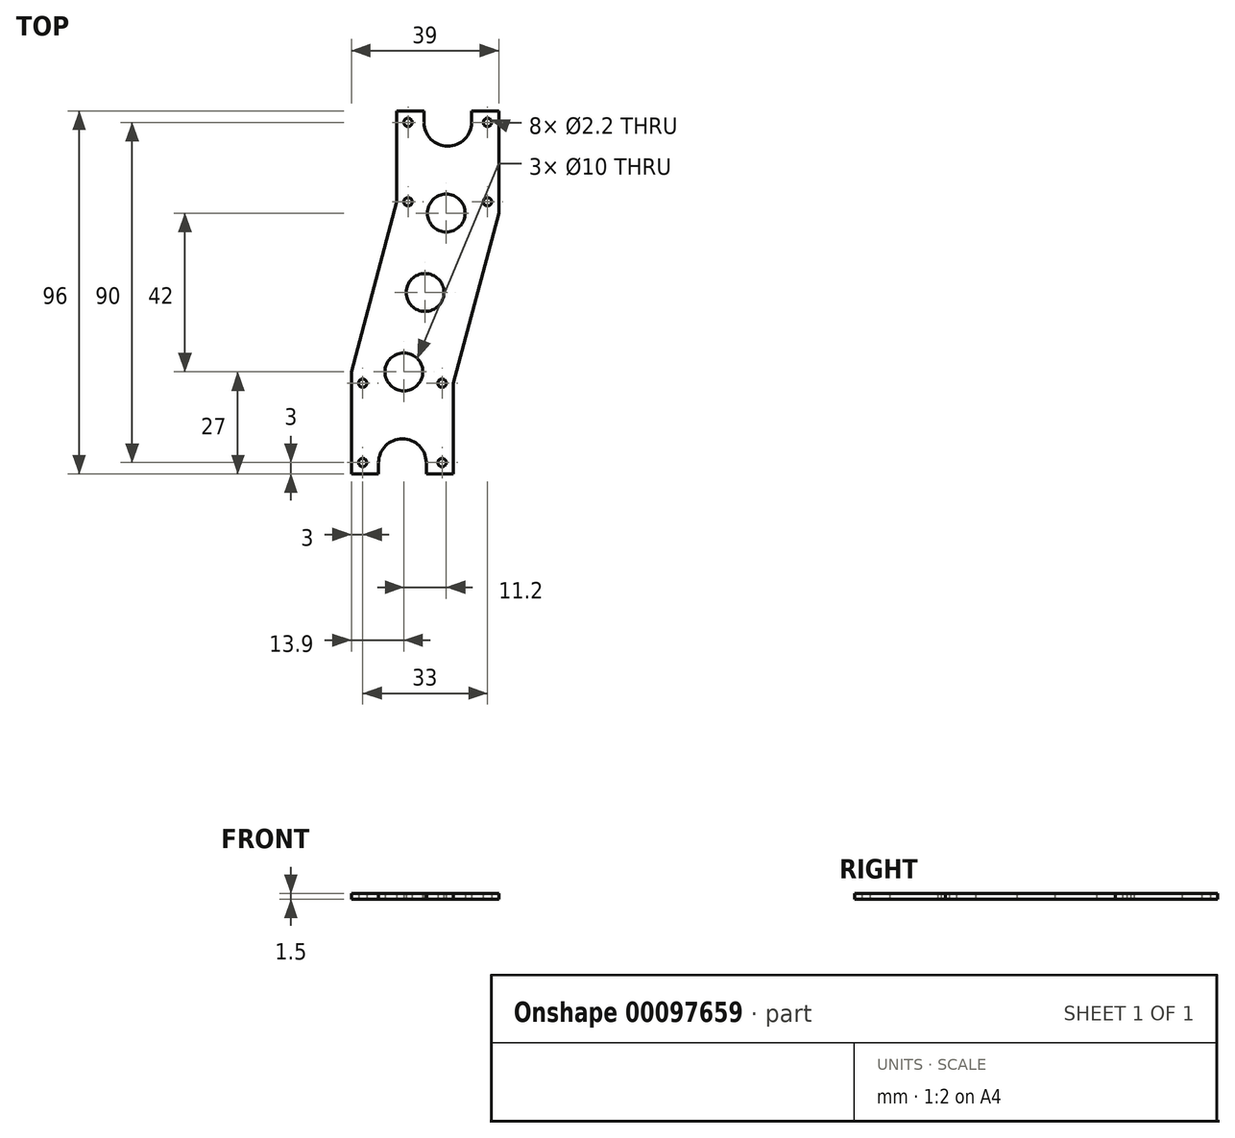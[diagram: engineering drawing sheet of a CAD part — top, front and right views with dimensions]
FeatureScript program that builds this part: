
annotation { "Feature Type Name" : "Feature", "Feature Type Description" : "" }
export const myFeature = defineFeature(function(context is Context, id is Id, definition is map)
    precondition{}
    {
        {
            var Q0;
            Q0=qCreatedBy(makeId("Top.planeOp"),FACE);
            var sketch = newSketch(context, id + "F0", { "sketchPlane" : qUnion([Q0])});
            skLineSegment(sketch, "E0.bottom", {"start": v(25.5, 48) * mm, "end": v(6.3, 48) * mm});
            skLineSegment(sketch, "E0.top", {"start": v(25.5, -48) * mm, "end": v(6.3, -48) * mm});
            skLineSegment(sketch, "E0.right", {"start": v(-25.5, 48) * mm, "end": v(-25.5, -48) * mm});
            skPoint(sketch, "E0.middle", {"position": v(0, 0) * mm});
            skArc(sketch, "E1", {"start": v(-6.3, 45) * mm, "mid": v(0, 38.7) * mm, "end": v(6.3, 45) * mm});
            skCircle(sketch, "E2", {"center": v(10.5, 45) * mm, "radius": 1.1 * mm});
            skCircle(sketch, "E3", {"center": v(10.5, 24) * mm, "radius": 1.1 * mm});
            skLineSegment(sketch, "E4", {"start": v(-6.3, 45) * mm, "end": v(-6.3, 48) * mm});
            skLineSegment(sketch, "E5", {"start": v(6.3, 45) * mm, "end": v(6.3, 48) * mm});
            skLineSegment(sketch, "E6.trimOffspring", {"start": v(-6.3, 48) * mm, "end": v(-25.5, 48) * mm});
            skCircle(sketch, "E7.MirrorC", {"center": v(-10.5, 45) * mm, "radius": 1.1 * mm});
            skCircle(sketch, "E8.MirrorC", {"center": v(-10.5, 24) * mm, "radius": 1.1 * mm});
            skLineSegment(sketch, "E9.left", {"start": v(25.5, 48) * mm, "end": v(25.5, -48) * mm});
            skCircle(sketch, "E10.MirrorC", {"center": v(-10.5, -24) * mm, "radius": 1.1 * mm});
            skCircle(sketch, "E11.MirrorC", {"center": v(10.5, -24) * mm, "radius": 1.1 * mm});
            skCircle(sketch, "E12.MirrorC", {"center": v(10.5, -45) * mm, "radius": 1.1 * mm});
            skCircle(sketch, "E13.MirrorC", {"center": v(-10.5, -45) * mm, "radius": 1.1 * mm});
            skArc(sketch, "E14.MirrorCS", {"start": v(-6.3, -45) * mm, "mid": v(0, -38.7) * mm, "end": v(6.3, -45) * mm});
            skLineSegment(sketch, "E15.MirrorCS", {"start": v(6.3, -45) * mm, "end": v(6.3, -48) * mm});
            skLineSegment(sketch, "E16.MirrorCS", {"start": v(-6.3, -45) * mm, "end": v(-6.3, -48) * mm});
            skLineSegment(sketch, "E17.trimOffspring", {"start": v(-18.3, -48) * mm, "end": v(-25.5, -48) * mm});
            skLineSegment(sketch, "E18", {"start": v(-5.7, -48) * mm, "end": v(6.3, -48) * mm});
            skLineSegment(sketch, "E19", {"start": v(-6, -48) * mm, "end": v(-6, 0) * mm, "construction": true});
            skLineSegment(sketch, "E20.MirrorCS", {"start": v(-5.7, -45) * mm, "end": v(-5.7, -48) * mm});
            skArc(sketch, "E21.MirrorCS", {"start": v(-5.7, -45) * mm, "mid": v(-12, -38.7) * mm, "end": v(-18.3, -45) * mm});
            skLineSegment(sketch, "E22.MirrorCS", {"start": v(-18.3, -45) * mm, "end": v(-18.3, -48) * mm});
            skCircle(sketch, "E23.MirrorC", {"center": v(-1.5, -45) * mm, "radius": 1.1 * mm});
            skCircle(sketch, "E24.MirrorC", {"center": v(-1.5, -24) * mm, "radius": 1.1 * mm});
            skCircle(sketch, "E25.MirrorC", {"center": v(-22.5, -24) * mm, "radius": 1.1 * mm});
            skCircle(sketch, "E26.MirrorC", {"center": v(-22.5, -45) * mm, "radius": 1.1 * mm});
            skSolve(sketch);
        }
        {
            var Q0;
            {var subQ1=sQuery(id+"F0.wireOp",EDGE,"E15.MirrorCS");Q0=makeQuery(id+"F0.imprint","IMPRINT",FACE,{"disambiguationData":[TD([[makeQuery(id+"F0.imprint","IMPRINT",EDGE,{"derivedFrom":subQ1}),-1.0]])]});}
            var Q1;
            Q1=makeQuery(id+"F0.imprint","IMPRINT",FACE,{"disambiguationData":[TD([[makeQuery(id+"F0.imprint","IMPRINT",EDGE,{"derivedFrom":sQuery(id+"F0.wireOp",EDGE,"E1")}),-1.0]])]});
            var Q2;
            Q2=makeQuery(id+"F0.imprint","IMPRINT",FACE,{"disambiguationData":[TD([[makeQuery(id+"F0.imprint","IMPRINT",EDGE,{"derivedFrom":sQuery(id+"F0.wireOp",EDGE,"E10.MirrorC")}),1.0]])]});
            var Q3;
            Q3=makeQuery(id+"F0.imprint","IMPRINT",FACE,{"disambiguationData":[TD([[makeQuery(id+"F0.imprint","IMPRINT",EDGE,{"derivedFrom":sQuery(id+"F0.wireOp",EDGE,"E12.MirrorC")}),-1.0]])]});
            var Q4;
            Q4=makeQuery(id+"F0.imprint","IMPRINT",FACE,{"disambiguationData":[TD([[makeQuery(id+"F0.imprint","IMPRINT",EDGE,{"derivedFrom":sQuery(id+"F0.wireOp",EDGE,"E11.MirrorC")}),-1.0]])]});
            extrude(context, id + "F1", {"entities" : qUnion([Q0, Q1, Q2, Q3, Q4]), "depth" : 1.5 * mm});
        }
        {
            var Q0;
            Q0=makeQuery(id+"F1.opExtrude","CAP_FACE",FACE,{"disambiguationData":[OSD([sQuery(id+"F0.wireOp",EDGE,"E1"),sQuery(id+"F0.wireOp",EDGE,"E2"),sQuery(id+"F0.wireOp",EDGE,"E3"),sQuery(id+"F0.wireOp",EDGE,"E4"),sQuery(id+"F0.wireOp",EDGE,"E5"),sQuery(id+"F0.wireOp",EDGE,"E7.MirrorC"),sQuery(id+"F0.wireOp",EDGE,"E8.MirrorC"),sQuery(id+"F0.wireOp",EDGE,"E0.bottom"),sQuery(id+"F0.wireOp",EDGE,"E0.top"),sQuery(id+"F0.wireOp",EDGE,"E9.left"),sQuery(id+"F0.wireOp",EDGE,"E0.right"),sQuery(id+"F0.wireOp",EDGE,"E6.trimOffspring"),sQuery(id+"F0.wireOp",EDGE,"E17.trimOffspring"),sQuery(id+"F0.wireOp",EDGE,"E18"),sQuery(id+"F0.wireOp",EDGE,"E20.MirrorCS"),sQuery(id+"F0.wireOp",EDGE,"E21.MirrorCS"),sQuery(id+"F0.wireOp",EDGE,"E22.MirrorCS"),sQuery(id+"F0.wireOp",EDGE,"E23.MirrorC"),sQuery(id+"F0.wireOp",EDGE,"E24.MirrorC"),sQuery(id+"F0.wireOp",EDGE,"E25.MirrorC"),sQuery(id+"F0.wireOp",EDGE,"E26.MirrorC")])],"isStart":true});
            var sketch = newSketch(context, id + "F2", { "sketchPlane" : qUnion([Q0])});
            skLineSegment(sketch, "E27.bottom", {"start": v(-25.5, 48) * mm, "end": v(-25.5, 48) * mm});
            skLineSegment(sketch, "E27.top", {"start": v(-25.5, -48) * mm, "end": v(-25.5, -48) * mm});
            skLineSegment(sketch, "E27.left", {"start": v(-25.5, 48) * mm, "end": v(-25.5, -48) * mm});
            skLineSegment(sketch, "E27.right", {"start": v(-25.5, 48) * mm, "end": v(-25.5, -48) * mm});
            skPoint(sketch, "E28", {"position": v(-22.5, 45) * mm});
            skPoint(sketch, "E29", {"position": v(10.5, -45) * mm});
            skPoint(sketch, "E30", {"position": v(-10.5, -24) * mm});
            skPoint(sketch, "E31", {"position": v(10.5, -24) * mm});
            skPoint(sketch, "E32", {"position": v(-10.5, -45) * mm});
            skPoint(sketch, "E33", {"position": v(-22.5, 24) * mm});
            skPoint(sketch, "E34", {"position": v(-1.5, 45) * mm});
            skPoint(sketch, "E35", {"position": v(-1.5, 24) * mm});
            skLineSegment(sketch, "E36.bottom", {"start": v(25.5, -48) * mm, "end": v(13.5, -48) * mm});
            skLineSegment(sketch, "E36.top", {"start": v(25.5, 48) * mm, "end": v(13.5, 48) * mm});
            skLineSegment(sketch, "E36.left", {"start": v(25.5, -48) * mm, "end": v(25.5, 48) * mm});
            skLineSegment(sketch, "E36.right", {"start": v(13.5, -48) * mm, "end": v(13.5, 48) * mm});
            skLineSegment(sketch, "E37.bottom", {"start": v(-25.5, -48) * mm, "end": v(-13.5, -48) * mm});
            skLineSegment(sketch, "E37.top", {"start": v(-25.5, -24) * mm, "end": v(-13.5, -24) * mm});
            skLineSegment(sketch, "E37.left", {"start": v(-25.5, -48) * mm, "end": v(-25.5, -24) * mm});
            skLineSegment(sketch, "E37.right", {"start": v(-13.5, -48) * mm, "end": v(-13.5, -24) * mm});
            skLineSegment(sketch, "E38.bottom", {"start": v(13.5, 48) * mm, "end": v(1.5, 48) * mm});
            skLineSegment(sketch, "E38.top", {"start": v(13.5, 24) * mm, "end": v(1.5, 24) * mm});
            skLineSegment(sketch, "E38.left", {"start": v(13.5, 48) * mm, "end": v(13.5, 24) * mm});
            skLineSegment(sketch, "E38.right", {"start": v(1.5, 48) * mm, "end": v(1.5, 24) * mm});
            skLineSegment(sketch, "E39", {"start": v(-25.5, 21) * mm, "end": v(-13.5, -24) * mm});
            skLineSegment(sketch, "E40", {"start": v(1.5, 24) * mm, "end": v(13.5, -21) * mm});
            skLineSegment(sketch, "E41.bottom", {"start": v(1.5, 24) * mm, "end": v(13.5, 24) * mm});
            skLineSegment(sketch, "E41.top", {"start": v(1.5, -21) * mm, "end": v(13.5, -21) * mm});
            skLineSegment(sketch, "E41.left", {"start": v(1.5, 24) * mm, "end": v(1.5, -21) * mm});
            skLineSegment(sketch, "E41.right", {"start": v(13.5, 24) * mm, "end": v(13.5, -21) * mm});
            skSolve(sketch);
        }
        {
            var Q0;
            {var subQ1=sQuery(id+"F2.wireOp",EDGE,"E27.bottom");Q0=makeQuery(id+"F2.imprint","IMPRINT",FACE,{"disambiguationData":[TD([[makeQuery(id+"F2.imprint","IMPRINT",EDGE,{"derivedFrom":subQ1}),1.0]])]});}
            var Q1;
            {var subQ0=sQuery(id+"F2.wireOp",EDGE,"E37.top");Q1=makeQuery(id+"F2.imprint","IMPRINT",FACE,{"disambiguationData":[TD([[makeQuery(id+"F2.imprint","IMPRINT",EDGE,{"derivedFrom":subQ0}),1.0]])]});}
            var Q2;
            {var subQ1=sQuery(id+"F2.wireOp",EDGE,"E36.bottom");Q2=makeQuery(id+"F2.imprint","IMPRINT",FACE,{"disambiguationData":[TD([[makeQuery(id+"F2.imprint","IMPRINT",EDGE,{"derivedFrom":subQ1}),-1.0]])]});}
            var Q3;
            Q3=makeQuery(id+"F2.imprint","IMPRINT",FACE,{"disambiguationData":[TD([[makeQuery(id+"F2.imprint","IMPRINT",EDGE,{"derivedFrom":sQuery(id+"F2.wireOp",EDGE,"E37.bottom")}),-1.0]])]});
            var Q4;
            Q4=makeQuery(id+"F2.imprint","IMPRINT",FACE,{"disambiguationData":[TD([[makeQuery(id+"F2.imprint","IMPRINT",EDGE,{"derivedFrom":sQuery(id+"F2.wireOp",EDGE,"E38.bottom")}),-1.0]])]});
            var Q5;
            Q5=makeQuery(id+"F2.imprint","IMPRINT",FACE,{"disambiguationData":[TD([[makeQuery(id+"F2.imprint","IMPRINT",EDGE,{"derivedFrom":sQuery(id+"F2.wireOp",EDGE,"E40")}),1.0]])]});
            extrude(context, id + "F3", {"entities" : qUnion([Q0, Q1, Q2, Q3, Q4, Q5]), "operationType" : NewBodyOperationType.REMOVE, "endBound" : BoundingType.UP_TO_NEXT, "oppositeDirection" : true, "depth" : 25 * mm});
        }
        {
            var Q0;
            Q0=makeQuery(id+"F1.opExtrude","CAP_FACE",FACE,{"disambiguationData":[OSD([sQuery(id+"F0.wireOp",EDGE,"E1"),sQuery(id+"F0.wireOp",EDGE,"E2"),sQuery(id+"F0.wireOp",EDGE,"E3"),sQuery(id+"F0.wireOp",EDGE,"E4"),sQuery(id+"F0.wireOp",EDGE,"E5"),sQuery(id+"F0.wireOp",EDGE,"E7.MirrorC"),sQuery(id+"F0.wireOp",EDGE,"E8.MirrorC"),sQuery(id+"F0.wireOp",EDGE,"E0.bottom"),sQuery(id+"F0.wireOp",EDGE,"E0.top"),sQuery(id+"F0.wireOp",EDGE,"E9.left"),sQuery(id+"F0.wireOp",EDGE,"E0.right"),sQuery(id+"F0.wireOp",EDGE,"E6.trimOffspring"),sQuery(id+"F0.wireOp",EDGE,"E17.trimOffspring"),sQuery(id+"F0.wireOp",EDGE,"E18"),sQuery(id+"F0.wireOp",EDGE,"E20.MirrorCS"),sQuery(id+"F0.wireOp",EDGE,"E21.MirrorCS"),sQuery(id+"F0.wireOp",EDGE,"E22.MirrorCS"),sQuery(id+"F0.wireOp",EDGE,"E23.MirrorC"),sQuery(id+"F0.wireOp",EDGE,"E24.MirrorC"),sQuery(id+"F0.wireOp",EDGE,"E25.MirrorC"),sQuery(id+"F0.wireOp",EDGE,"E26.MirrorC")])],"isStart":true});
            var sketch = newSketch(context, id + "F4", { "sketchPlane" : qUnion([Q0])});
            skLineSegment(sketch, "E42", {"start": v(13.5, -21) * mm, "end": v(-14.3, -21) * mm, "construction": true});
            skLineSegment(sketch, "E43", {"start": v(-25.5, 21) * mm, "end": v(2.3, 21) * mm, "construction": true});
            skLineSegment(sketch, "E44", {"start": v(-0.4, -21) * mm, "end": v(-11.6, 21) * mm, "construction": true});
            skCircle(sketch, "E45", {"center": v(-0.4, -21) * mm, "radius": 5 * mm});
            skCircle(sketch, "E46", {"center": v(-11.6, 21) * mm, "radius": 5 * mm});
            skCircle(sketch, "E47", {"center": v(-6, 0) * mm, "radius": 5 * mm});
            skSolve(sketch);
        }
        {
            var Q0;
            Q0=qSketchRegion(id+"F4",true);
            extrude(context, id + "F5", {"entities" : qUnion([Q0]), "operationType" : NewBodyOperationType.REMOVE, "endBound" : BoundingType.UP_TO_NEXT, "oppositeDirection" : true, "depth" : 25 * mm});
        }
    });
